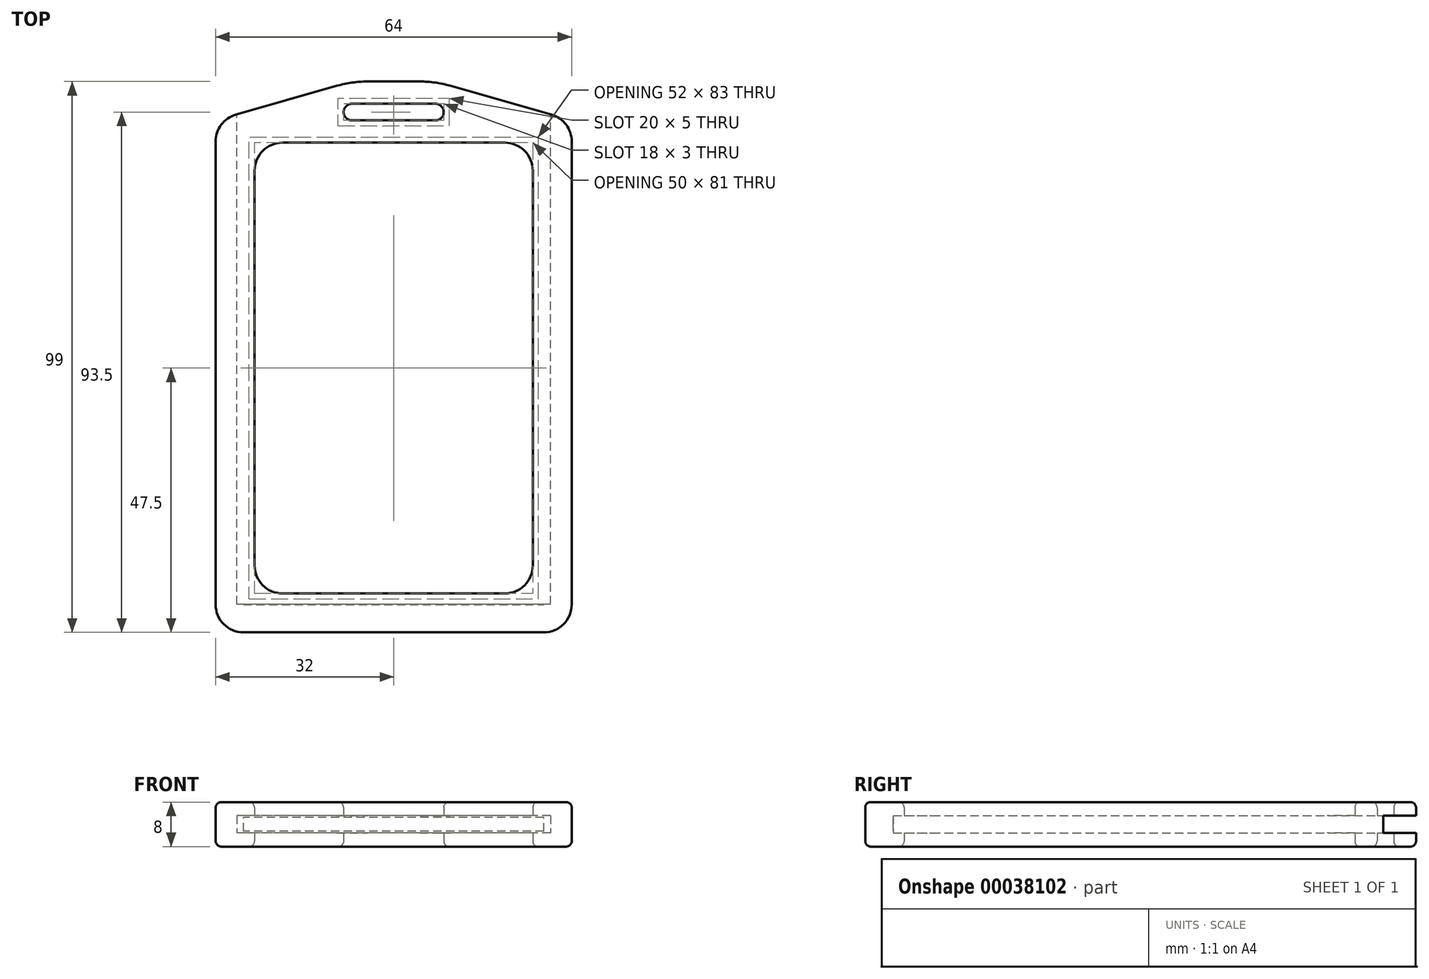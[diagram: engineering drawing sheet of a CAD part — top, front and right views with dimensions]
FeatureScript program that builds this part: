
annotation { "Feature Type Name" : "Feature", "Feature Type Description" : "" }
export const myFeature = defineFeature(function(context is Context, id is Id, definition is map)
    precondition{}
    {
        {
            var Q0;
            Q0=qCreatedBy(makeId("Top.planeOp"),FACE);
            var sketch = newSketch(context, id + "F0", { "sketchPlane" : qUnion([Q0])});
            skLineSegment(sketch, "E0.rect.bottom", {"start": v(-27, 42.5) * mm, "end": v(27, 42.5) * mm});
            skLineSegment(sketch, "E0.rect.top", {"start": v(-27, -42.5) * mm, "end": v(27, -42.5) * mm});
            skLineSegment(sketch, "E0.rect.left", {"start": v(-27, 42.5) * mm, "end": v(-27, -42.5) * mm});
            skLineSegment(sketch, "E0.rect.right", {"start": v(27, 42.5) * mm, "end": v(27, -42.5) * mm});
            skPoint(sketch, "E0.rect.middle", {"position": v(0, 0) * mm});
            skSolve(sketch);
        }
        {
            var Q0;
            Q0=makeQuery(id+"F0.imprint","IMPRINT",FACE,{"disambiguationData":[TD([[makeQuery(id+"F0.imprint","IMPRINT",EDGE,{"derivedFrom":sQuery(id+"F0.wireOp",EDGE,"E0.rect.bottom")}),-1.0]])]});
            extrude(context, id + "F1", {"entities" : qUnion([Q0]), "depth" : 2.5 * mm});
        }
        {
            var Q0;
            Q0=qCreatedBy(makeId("Top.planeOp"),FACE);
            var sketch = newSketch(context, id + "F2", { "sketchPlane" : qUnion([Q0])});
            skLineSegment(sketch, "E1", {"start": v(-32, -47.5) * mm, "end": v(-32, 44.5) * mm});
            skLineSegment(sketch, "E2", {"start": v(32, 44.5) * mm, "end": v(32, -47.5) * mm});
            skLineSegment(sketch, "E3", {"start": v(32, -47.5) * mm, "end": v(-32, -47.5) * mm});
            skLineSegment(sketch, "E4", {"start": v(-7.5, 47.5) * mm, "end": v(7.5, 47.5) * mm});
            skLineSegment(sketch, "E5", {"start": v(-7.5, 44.5) * mm, "end": v(7.5, 44.5) * mm});
            skArc(sketch, "E6", {"start": v(-7.5, 47.5) * mm, "mid": v(-9, 46) * mm, "end": v(-7.5, 44.5) * mm});
            skArc(sketch, "E7", {"start": v(7.5, 47.5) * mm, "mid": v(9, 46) * mm, "end": v(7.5, 44.5) * mm});
            skLineSegment(sketch, "E8.rect.bottom", {"start": v(-25, 40.5) * mm, "end": v(25, 40.5) * mm});
            skLineSegment(sketch, "E8.rect.top", {"start": v(-25, -40.5) * mm, "end": v(25, -40.5) * mm});
            skLineSegment(sketch, "E8.rect.left", {"start": v(-25, 40.5) * mm, "end": v(-25, -40.5) * mm});
            skLineSegment(sketch, "E8.rect.right", {"start": v(25, 40.5) * mm, "end": v(25, -40.5) * mm});
            skPoint(sketch, "E8.rect.middle", {"position": v(0, 0) * mm});
            skLineSegment(sketch, "E9", {"start": v(-32, 44.5) * mm, "end": v(-7.5, 51.5) * mm});
            skLineSegment(sketch, "E10", {"start": v(-7.5, 51.5) * mm, "end": v(7.5, 51.5) * mm});
            skLineSegment(sketch, "E11", {"start": v(7.5, 51.5) * mm, "end": v(32, 44.5) * mm});
            skSolve(sketch);
        }
        {
            var Q0;
            Q0=makeQuery(id+"F2.imprint","IMPRINT",FACE,{"disambiguationData":[TD([[makeQuery(id+"F2.imprint","IMPRINT",EDGE,{"derivedFrom":sQuery(id+"F2.wireOp",EDGE,"E1")}),-1.0]])]});
            var Q1;
            Q1=makeQuery(id+"F2.imprint","IMPRINT",FACE,{"disambiguationData":[TD([[makeQuery(id+"F2.imprint","IMPRINT",EDGE,{"derivedFrom":sQuery(id+"F2.wireOp",EDGE,"E8.rect.bottom")}),1.0]])]});
            extrude(context, id + "F3", {"entities" : qUnion([Q0, Q1]), "depth" : 8 * mm});
        }
        {
            var Q0;
            Q0=makeQuery(id+"F3.opExtrude","SWEPT_EDGE",EDGE,{"disambiguationData":[OSD([sQuery(id+"F2.wireOp",EDGE,"E1"),sQuery(id+"F2.wireOp",EDGE,"bdb59242-d5a5-46b9-b7b7-c48a45b36775")])]});
            var Q1;
            Q1=makeQuery(id+"F3.opExtrude","SWEPT_EDGE",EDGE,{"disambiguationData":[OSD([sQuery(id+"F2.wireOp",EDGE,"daee0165-ca23-428e-b79d-c411e0a02959"),sQuery(id+"F2.wireOp",EDGE,"E2")])]});
            var Q2;
            Q2=makeQuery(id+"F3.opExtrude","SWEPT_EDGE",EDGE,{"disambiguationData":[OSD([sQuery(id+"F2.wireOp",EDGE,"E2"),sQuery(id+"F2.wireOp",EDGE,"E3")])]});
            var Q3;
            Q3=makeQuery(id+"F3.opExtrude","SWEPT_EDGE",EDGE,{"disambiguationData":[OSD([sQuery(id+"F2.wireOp",EDGE,"E1"),sQuery(id+"F2.wireOp",EDGE,"E3")])]});
            fillet(context, id + "F4", {"entities" : qUnion([Q0, Q1, Q2, Q3]), "radius" : 5 * mm, "tangentPropagation" : true, "allowEdgeOverflow" : false});
        }
        {
            var Q0;
            Q0=makeQuery(id+"F3.opExtrude","SWEPT_EDGE",EDGE,{"disambiguationData":[OSD([sQuery(id+"F2.wireOp",EDGE,"E9"),sQuery(id+"F2.wireOp",EDGE,"E10")])]});
            var Q1;
            Q1=makeQuery(id+"F3.opExtrude","SWEPT_EDGE",EDGE,{"disambiguationData":[OSD([sQuery(id+"F2.wireOp",EDGE,"E10"),sQuery(id+"F2.wireOp",EDGE,"E11")])]});
            fillet(context, id + "F5", {"entities" : qUnion([Q0, Q1]), "radius" : 20 * mm, "tangentPropagation" : true, "allowEdgeOverflow" : false});
        }
        {
            var Q0;
            Q0=makeQuery(id+"F3.opExtrude","CAP_EDGE",EDGE,{"disambiguationData":[OSD([sQuery(id+"F2.wireOp",EDGE,"E4")])],"isStart":false});
            var Q1;
            Q1=makeQuery(id+"F3.opExtrude","CAP_EDGE",EDGE,{"disambiguationData":[OSD([sQuery(id+"F2.wireOp",EDGE,"E4")])],"isStart":true});
            fillet(context, id + "F6", {"entities" : qUnion([Q0, Q1]), "radius" : 1 * mm, "tangentPropagation" : true, "allowEdgeOverflow" : false});
        }
        {
            var Q0;
            Q0=makeQuery(id+"F3.opExtrude","SWEPT_EDGE",EDGE,{"disambiguationData":[OSD([sQuery(id+"F2.wireOp",EDGE,"E8.rect.bottom"),sQuery(id+"F2.wireOp",EDGE,"E8.rect.left")])]});
            var Q1;
            Q1=makeQuery(id+"F3.opExtrude","SWEPT_EDGE",EDGE,{"disambiguationData":[OSD([sQuery(id+"F2.wireOp",EDGE,"E8.rect.bottom"),sQuery(id+"F2.wireOp",EDGE,"E8.rect.right")])]});
            var Q2;
            Q2=makeQuery(id+"F3.opExtrude","SWEPT_EDGE",EDGE,{"disambiguationData":[OSD([sQuery(id+"F2.wireOp",EDGE,"E8.rect.top"),sQuery(id+"F2.wireOp",EDGE,"E8.rect.right")])]});
            var Q3;
            Q3=makeQuery(id+"F3.opExtrude","SWEPT_EDGE",EDGE,{"disambiguationData":[OSD([sQuery(id+"F2.wireOp",EDGE,"E8.rect.top"),sQuery(id+"F2.wireOp",EDGE,"E8.rect.left")])]});
            fillet(context, id + "F7", {"entities" : qUnion([Q0, Q1, Q2, Q3]), "radius" : 5 * mm, "tangentPropagation" : true, "allowEdgeOverflow" : false});
        }
        {
            var Q0;
            Q0=makeQuery(id+"F3.opExtrude","CAP_EDGE",EDGE,{"disambiguationData":[OSD([sQuery(id+"F2.wireOp",EDGE,"E8.rect.bottom")])],"isStart":false});
            var Q1;
            Q1=makeQuery(id+"F3.opExtrude","CAP_EDGE",EDGE,{"disambiguationData":[OSD([sQuery(id+"F2.wireOp",EDGE,"E8.rect.bottom")])],"isStart":true});
            var Q2;
            {var subQ0=sQuery(id+"F2.wireOp",EDGE,"E1");var subQ1=sQuery(id+"F2.wireOp",EDGE,"E3");Q2=makeQuery(id+"F4.opFillet","BLEND_EDGE",EDGE,{"blendedFrom":[makeQuery(id+"F3.opExtrude","SWEPT_EDGE",EDGE,{"disambiguationData":[OSD([subQ0,subQ1])]}),makeQuery(id+"F3.opExtrude","CAP_FACE",FACE,{"disambiguationData":[OSD([subQ0,sQuery(id+"F2.wireOp",EDGE,"bdb59242-d5a5-46b9-b7b7-c48a45b36775"),sQuery(id+"F2.wireOp",EDGE,"823fc3bd-2c2f-4f9b-bb1d-b0eb3bebb9c6"),sQuery(id+"F2.wireOp",EDGE,"daee0165-ca23-428e-b79d-c411e0a02959"),sQuery(id+"F2.wireOp",EDGE,"E2"),subQ1,sQuery(id+"F2.wireOp",EDGE,"E4"),sQuery(id+"F2.wireOp",EDGE,"E5"),sQuery(id+"F2.wireOp",EDGE,"E6"),sQuery(id+"F2.wireOp",EDGE,"E7"),sQuery(id+"F2.wireOp",EDGE,"E8.rect.bottom"),sQuery(id+"F2.wireOp",EDGE,"E8.rect.top"),sQuery(id+"F2.wireOp",EDGE,"E8.rect.left"),sQuery(id+"F2.wireOp",EDGE,"E8.rect.right")])],"isStart":false})],"blendedInto":[makeQuery(id+"F3.opExtrude","CAP_FACE",FACE,{"disambiguationData":[OSD([subQ0,sQuery(id+"F2.wireOp",EDGE,"bdb59242-d5a5-46b9-b7b7-c48a45b36775"),sQuery(id+"F2.wireOp",EDGE,"823fc3bd-2c2f-4f9b-bb1d-b0eb3bebb9c6"),sQuery(id+"F2.wireOp",EDGE,"daee0165-ca23-428e-b79d-c411e0a02959"),sQuery(id+"F2.wireOp",EDGE,"E2"),subQ1,sQuery(id+"F2.wireOp",EDGE,"E4"),sQuery(id+"F2.wireOp",EDGE,"E5"),sQuery(id+"F2.wireOp",EDGE,"E6"),sQuery(id+"F2.wireOp",EDGE,"E7"),sQuery(id+"F2.wireOp",EDGE,"E8.rect.bottom"),sQuery(id+"F2.wireOp",EDGE,"E8.rect.top"),sQuery(id+"F2.wireOp",EDGE,"E8.rect.left"),sQuery(id+"F2.wireOp",EDGE,"E8.rect.right")])],"isStart":false})]});}
            var Q3;
            Q3=makeQuery(id+"F3.opExtrude","CAP_EDGE",EDGE,{"disambiguationData":[OSD([sQuery(id+"F2.wireOp",EDGE,"E3")])],"isStart":true});
            fillet(context, id + "F8", {"entities" : qUnion([Q0, Q1, Q2, Q3]), "radius" : 1 * mm, "tangentPropagation" : true, "allowEdgeOverflow" : false});
        }
        {
            var Q0;
            Q0=makeQuery(id+"F1.opExtrude","SWEPT_BODY",BODY,{"disambiguationData":[OSD([sQuery(id+"F0.wireOp",EDGE,"E0.rect.bottom"),sQuery(id+"F0.wireOp",EDGE,"E0.rect.top"),sQuery(id+"F0.wireOp",EDGE,"E0.rect.left"),sQuery(id+"F0.wireOp",EDGE,"E0.rect.right")])]});
            transform(context, id + "F9", {"entities" : qUnion([Q0]), "transformType" : TransformType.TRANSLATION_3D, "dx" : 0 * mm, "dy" : 0 * mm, "dz" : 2.75 * mm, "makeCopy" : false});
        }
        {
            var Q0;
            Q0=makeQuery(id+"F3.opExtrude","SWEPT_FACE",FACE,{"disambiguationData":[OSD([sQuery(id+"F2.wireOp",EDGE,"E10")])]});
            var sketch = newSketch(context, id + "F10", { "sketchPlane" : qUnion([Q0])});
            skLineSegment(sketch, "E12.bottom", {"start": v(-28.2, 5.55) * mm, "end": v(28.2, 5.55) * mm});
            skLineSegment(sketch, "E12.top", {"start": v(-28.2, 2.45) * mm, "end": v(28.2, 2.45) * mm});
            skLineSegment(sketch, "E12.left", {"start": v(-28.2, 5.55) * mm, "end": v(-28.2, 2.45) * mm});
            skLineSegment(sketch, "E12.right", {"start": v(28.2, 5.55) * mm, "end": v(28.2, 2.45) * mm});
            skSolve(sketch);
        }
        {
            var Q0;
            Q0 = qSketchRegion(id + "F10", true);
            extrude(context, id + "F11", {"entities" : qUnion([Q0]), "operationType" : NewBodyOperationType.REMOVE, "oppositeDirection" : true, "depth" : 93.95 * mm});
        }
    });
